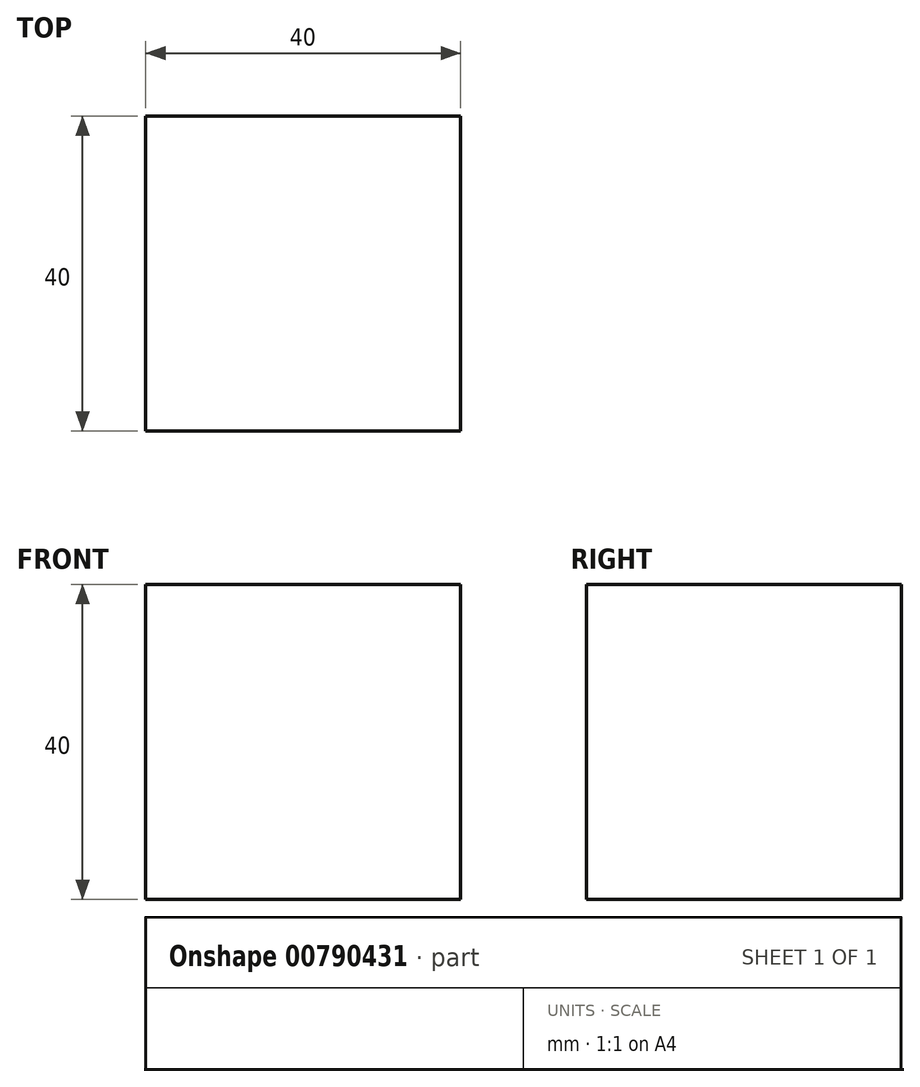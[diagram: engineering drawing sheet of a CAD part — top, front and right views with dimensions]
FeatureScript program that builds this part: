
annotation { "Feature Type Name" : "Feature", "Feature Type Description" : "" }
export const myFeature = defineFeature(function(context is Context, id is Id, definition is map)
    precondition{}
    {
        {
            var Q0;
            Q0=qCreatedBy(makeId("Front.planeOp"),FACE);
            var sketch = newSketch(context, id + "F0", { "sketchPlane" : qUnion([Q0])});
            skLineSegment(sketch, "E0.bottom", {"start": v(0, 0) * mm, "end": v(40, 0) * mm});
            skLineSegment(sketch, "E0.top", {"start": v(0, 40) * mm, "end": v(40, 40) * mm});
            skLineSegment(sketch, "E0.left", {"start": v(0, 0) * mm, "end": v(0, 40) * mm});
            skLineSegment(sketch, "E0.right", {"start": v(40, 0) * mm, "end": v(40, 40) * mm});
            skSolve(sketch);
        }
        {
            var Q0;
            Q0=makeQuery(id+"F0.imprint","IMPRINT",FACE,{"disambiguationData":[TD([[makeQuery(id+"F0.imprint","IMPRINT",EDGE,{"derivedFrom":sQuery(id+"F0.wireOp",EDGE,"E0.bottom")}),1.0]])]});
            extrude(context, id + "F1", {"entities" : qUnion([Q0]), "depth" : 40 * mm, "offsetDistance" : 25 * mm});
        }
        {
            var Q0;
            Q0=makeQuery(id+"F1.opExtrude","SWEPT_FACE",FACE,{"disambiguationData":[OSD([sQuery(id+"F0.wireOp",EDGE,"E0.top")])]});
            var sketch = newSketch(context, id + "F2", { "sketchPlane" : qUnion([Q0])});
            skCircle(sketch, "E1", {"center": v(20, -20) * mm, "radius": 8.23 * mm});
            skPoint(sketch, "E1.centerSnap0", {"position": v(40, -20) * mm});
            skPoint(sketch, "E1.centerSnap1", {"position": v(20, 0) * mm});
            skSolve(sketch);
        }
        {
            var Q0;
            Q0=makeQuery(id+"F2.imprint","IMPRINT",FACE,{"disambiguationData":[TD([[makeQuery(id+"F2.imprint","IMPRINT",EDGE,{"derivedFrom":sQuery(id+"F2.wireOp",EDGE,"E1")}),1.0]])]});
            extrude(context, id + "F3", {"entities" : qUnion([Q0]), "operationType" : NewBodyOperationType.ADD, "oppositeDirection" : true, "depth" : 25 * mm, "offsetDistance" : 25 * mm});
        }
    });
